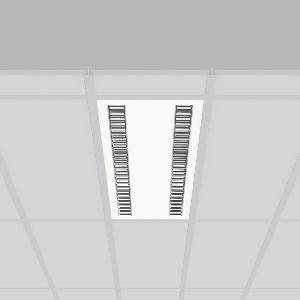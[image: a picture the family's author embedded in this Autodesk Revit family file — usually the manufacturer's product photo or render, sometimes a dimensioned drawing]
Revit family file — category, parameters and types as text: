
# Revit family: sonis_901682_002_1_76_2f35
name_source: partatom
category: Lighting Fixtures
units: mm (PartAtom-declared; Revit-internal decimal feet)

## family parameters
Cut with Voids When Loaded = No
Host = Face
Light Source = No
Part Type = Normal
Room Calculation Point = No
Round Connector Dimension = Use Diameter
Shared = No

## types (1)
- SONIS (1 x LED Modul 840, 6500 lm, 4000)
    Apparent Load = 50 VA
    CIE Flux Codes = 83 100 100 100 100
    Color Rendering = 80
    Color Temperature = 4000
    Default Elevation = 1800 mm
    Description = Series: SONIS
High-efficiency lay-in luminaire for ceiling systems with visible mounting rails. Housing: metal, powder-coated. Alea optical system: Reflector structure (ABS, Aluminium-coated, highly polished) with integrated diffuser made of non-yellowing plastic (PMMA) opal for glare-free light at the workstation. Narrow beam, brilliant luminous effect. Suitable for Recessed ceiling mounting. Driver integrated. Perfect for office areas (RUG < 19) and environments with computer screens in accordance with EN 12464-1. 
Colour: white
Length: 1247 mm
Width: 310 mm
Cut-out length: 1225 mm
Cut-out width: 285 mm
Recess height: 27 mm
Lamp: LED
Socket: without socket
Colour temperature: 4000K
Colour rendering index (CRI): 80
System power: 50 W
Rated luminous flux: 6500 lm
Luminous efficiency: 130 lm/W
Control gear: Converter, dimmable, DALI
Protection class: I
Type of protection: IP 20
    Height = 0 mm  [stored 0 ft]
    Lamp = 1 x LED Modul 840
    Lamp Light Flux = 6500 lm
    Lamp count = 1
    Length = 1247 mm
    Lifetime = 50000 h
    Luminous efficacy = 130 lm/W
    Manufacturer = RZB
    ModVariant = No
    Model = 901682.002.1.76
    Mounting Place = Ceiling
    Mounting Type = Recessed
    Number of Poles = 1
    OnlyDefault = Yes
    Power Factor = 1
    Product Name = SONIS
    Product group = Recessed modular luminaires
    ProductGroupID = 406
    Protection Class = Protection class I
    Protection Degree = IP 20
    RLX_Detail_Level = 1
    RLX_Emergency_Light_Flux = 0 lm
    RLX_Emergency_Type = 0
    RLX_Emergency_Type_DB = No
    RlxData = <blob elided: 37341 chars, md5=cbb0bc0e>
    Socket = socket
    Standby Power = 0 W
    System Light Flux = 6500 lm
    System Power = 50 W
    Type Comments = Product without accessories
    Type Image = 901649.002.jpg
    URL = http://relux.com
    VarID = ---
    Voltage = 0 V
    Weight = 0.00 kg
    Width = 310 mm

note: [stored X ft] marks values corroborated as IEEE doubles in the binary element streams (Revit-internal decimal feet)

## geometry (parser evidence)
native form markers: Blend x4, Sweep x10
no freeform markers — native parametric forms only
